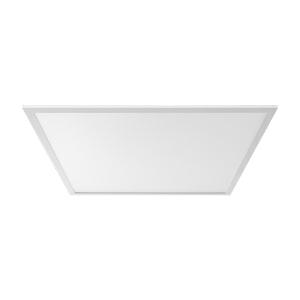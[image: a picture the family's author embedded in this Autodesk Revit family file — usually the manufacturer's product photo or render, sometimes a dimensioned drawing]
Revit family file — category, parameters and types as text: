
# Revit family: 3f_filippi_-_3f_led_panel_3f_filippi_-_22790_a01486_-_3flp6060ugr-830__1100ma____dali_0439
name_source: partatom
category: Lighting Fixtures
units: mm (PartAtom-declared; Revit-internal decimal feet)

## family parameters
Cut with Voids When Loaded = No
Host = Face
Light Source = No
Part Type = Normal
Room Calculation Point = No
Round Connector Dimension = Use Diameter
Shared = No

## types (1)
- 3F Filippi - 3F LED Panel (1 x LED, 4860 lm, 43 W, 3000 K)
    Apparent Load = 43 VA
    Approval mark = ENEC
    CIE Flux Codes = 63 89 97 100 100
    Color Rendering = 80
    Color Temperature = 3000 K
    Control Gear = Electronic transformer
    Default Elevation = 1800 mm
    Description = ILLUMINOTECHNICAL
Luminous efficiency 100% (DLOR 100%, ULOR 0%).
Initial luminous flux of the luminaire 4860 lm.
Direct symmetric distribution.
Installation Interdistance Transv.D = 1.18 x hu - Long.D = 1.30 x hu.
Average luminance <3000 cd/m² for radial angles >65°.
Tabular UGR (CIE 117 - 4H-8H; S=0.25H; 70/50/20): RUG 18.8 - 19.
Beam angle: 86° - 90°.
Luminous efficacy 113 lm/W.
Lifetime (L93/B10): 30000 h. (tq+25°C)
Lifetime (L90/B10): 50000 h. (tq+25°C)
Lifetime (L80/B10): 80000 h. (tq+25°C)
Lifetime (L75/B10): 100000 h. (tq+25°C)
Sudden decreased luminous flux after 50000 hours: 0% (C0).
Photobiological safety in compliance with IEC/TR 62778: RG0 risk exempt, (IEC 62471).
In compliance with IEC/EN 62722-2-1 - IEC/EN 62717 standards.

SOURCE
2 linear LED modules 830.
Energy efficiency class (UE 2019/2020 - UE 2019/2015): C.
CIE 13.3 Colour rendering index: CRI >80 (R9 <50%).
IES TM-30 Fidelity Index: Rf = 82 Rg = 95.
CCT nominal colour temperature 3000 K.
Colour initial tolerance (MacAdam): SDCM 3.

MECHANICAL
Housing in white painted epoxy-polyester powder aluminium.
Diffuser in SMP trasparent microprismatic methacrylate (PMMA) externally, anti-glare with high transmittance.
Perimetral frame in white polycarbonate.
Anti-fall safety cable.
Luminaire with limited surface temperature. - D - (EN 60598-2-24)
Dimensions: 595x595 mm, height 9 mm. Weight 2.505 kg.
IP43 protection degree for exposed part, IP20 for recessed part.
Mechanical strength to impacts IK06 (1 joule).
Glow-wire test resistance 650°C.

ELECTRICAL
Wiring on a separate unit (Multi-current power supply, to be ordered separately).
Power of the luminaire 43 W.
CE - IEC 60598-1 - EN 60598-1.
SAFE FLICKER: PstLM=<1 and SVM=<0.4 (IEC TR 61547-1 and IEC TR 63158), to ensure a more comfortable and safe light.
Luminaire compliant with EN 60598-2-22 for power supply from a centralised emergency system CPSS (Central Power Supply System), not incorporated in the luminaire - high risk areas excluded. The default power and flux are 100% in AC and 100% in DC.
Ambient temperature from 0°C to +25°C.
Temperature class T6 max 85°C.
Relative humidity UR: <85%.

INSTALLATION
Lay-in recessed fitting / Pull-up recessed fitting with brackets / Ceiling installation with frame / Suspension via accessory.
All accessories dedicated to this product are available on the Catalog and on our website www.3F-Filippi.com.

ACCESSORIES
A01486 - DELT40C-MEL DRIVER DALI DIP-SWITCH.
DALI, PUSH-DIM, electronic wiring 230V-50/60Hz, power factor 0.95 at full load, constant output current, SELV, class II, 1 driver, 1 DALI addresse.
Multi-current power supply that allows you to choose the driving current of the fixture at the time of installation (default 900mA) according to the required illuminance.
Quick connection non-reversible plug-socket terminal block, also for cascade connection.

APPLICATIONS
Suitable product for food production plants (HACCP), IFS (Food Version 6), BRC (GSFS Food Version 7).
Environments: with VDTs, meeting rooms, offices.
Environments: recreational, transit areas, corridors, schools, stairwells.
Environments where soft diffuse light is required for optimal visual comfort.

WARNING
Luminaire designed for disposal/recycling at end-of-life.
Replaceable control gear by a professional.
    Height = 0 mm  [stored 0 ft]
    Lamp = 1 x LED
    Lamp Light Flux = 4860 lm
    Lamp Power = 43 W
    Lamp count = 1
    Length = 595 mm
    Lifetime = 50000 h
    Luminous efficacy = 113 lm/W
    Manufacturer = 3F Filippi
    ModVariant = No
    Model = 3F Filippi - 22790+A01486 - 3FLP6060UGR-830 (1100mA) + DALI
    Mounting Place = Ceiling
    Mounting Type = Recessed
    Number of Poles = 1
    OnlyDefault = Yes
    Power Factor = 1
    Product Name = 3F Filippi - 3F LED Panel
    Product group = recessed luminaire
    ProductGroupID = 4
    Protection Class = Protection class II
    Protection Degree = IP 20
    RLX_Detail_Level = 1
    RLX_Emergency_Light_Flux = 0 lm
    RLX_Emergency_Type = 0
    RLX_Emergency_Type_DB = No
    RlxData = <blob elided: 32077 chars, md5=ef3de89f>
    Socket = socket
    Standby Power = 0 W
    System Light Flux = 4860 lm
    System Power = 43 W
    Type Comments = Product without accessories
    Type Image = 3ffilippi_3f_led_panel_596x596.jpg
    URL = http://relux.com
    VarID = ---
    Voltage = 0 V
    Weight = 0.00 kg
    Width = 595 mm

note: [stored X ft] marks values corroborated as IEEE doubles in the binary element streams (Revit-internal decimal feet)

## geometry (parser evidence)
native form markers: Blend x4, Sweep x10
no freeform markers — native parametric forms only
